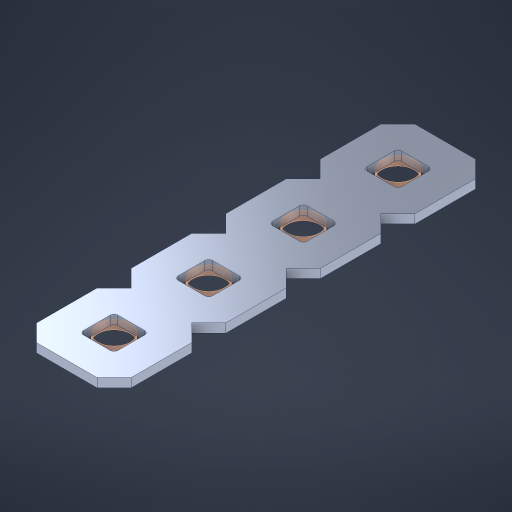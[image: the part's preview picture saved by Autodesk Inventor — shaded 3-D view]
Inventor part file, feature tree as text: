
AUTODESK INVENTOR PART (.ipt)
format: ipt  version: 2023 (Build 270158000, 158)  size: 310,272 bytes
history: native  units: in
note: dims shown in document units (in); Inventor stores cm internally (conversion verified against a paired STEP export)
features: other x5, extrude x3, sketch x2, pattern_linear x1
ambient origin geometry x8: Origin, YZ Plane, XZ Plane, XY Plane, X Axis, Y Axis, Z Axis, Center Point
bodies: Solid1 (feature_tree), Body (feature_tree)
feature tree (11):
  pattern_linear  "Rectangular Pattern1"  Spacing1=0.09in  [1 undecoded]
  sketch  "Sketch1"  dims[d1=0.5in]
  sketch  "Sketch2"  dims[d2=0.182in d3=0.09in d4=0.09in d5=0.09in d6=0.09in d7=0.09in d8=0.09in d9=0.09in d10=0.09in d11=0.02in d13=0.0in d14=0.172in d15=0.0625in d16=0.0in d19=0.5in d22=0.5in]
  other  "Srf1"
  other  "Srf126"
  other  "Srf127"
  other  "Srf128"
  other  "Circle"
  extrude  "ExtrusionSrf126"  Depth=0.09in
  extrude  "ExtrusionSrf127"  Depth=0.09in
  extrude  "ExtrusionSrf128"  Depth=0.09in
note: 1 required parameter value undecoded (feature->parameter linkage not recoverable at this tier; creation-order binding heuristic only, values carry confidence <= 0.55)
